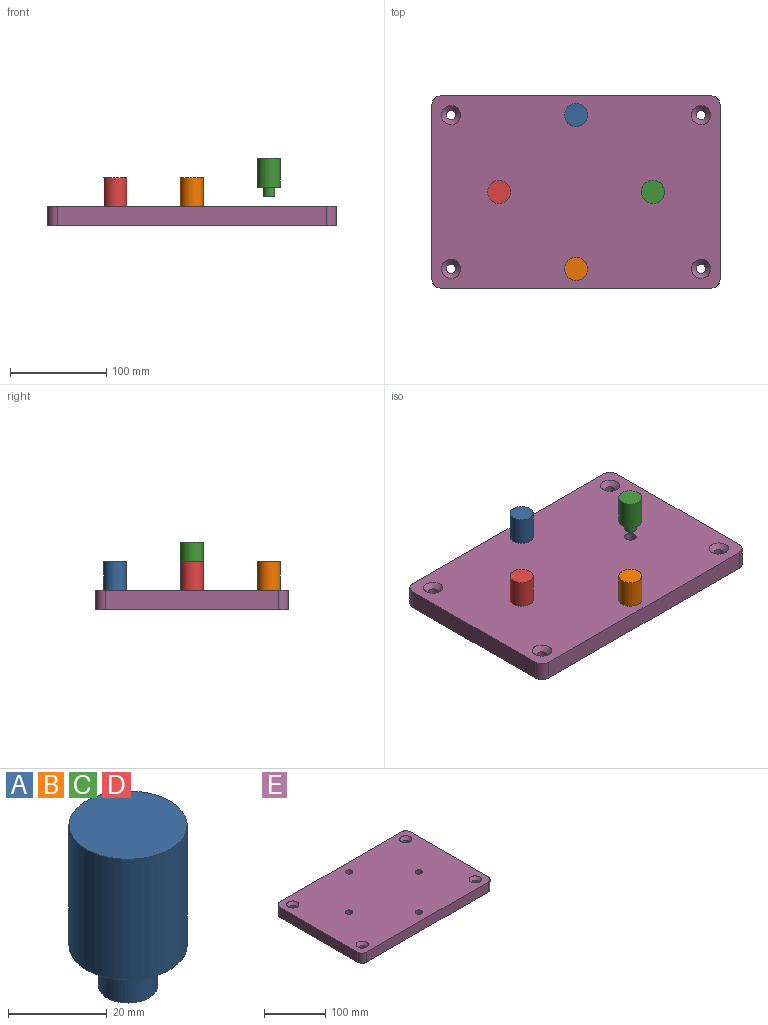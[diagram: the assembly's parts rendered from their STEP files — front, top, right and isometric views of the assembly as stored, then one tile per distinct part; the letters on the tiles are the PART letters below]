
ASSEMBLY  parts=5 mates=4
PART A: 5 faces, bbox 24x24x40 mm
  f0: plane 12x12mm, normal (0,0,-1), area 113.1mm2, adj f1
  f1: cylinder r=6mm len=12mm, axis (0,0,1), area 377mm2, adj f0,f2
  f2: plane 24x24mm, normal (0,0,-1), area 339.3mm2, adj f1,f3
  f3: cylinder r=12mm len=30mm, axis (0,0,1), area 2261.9mm2, adj f2,f4
  f4: plane 24x24mm, normal (0,0,1), area 452.4mm2, adj f3
PART B: same geometry as A
PART C: same geometry as A
PART D: same geometry as A
PART E: 26 faces, bbox 300x200x20 mm
  f0: plane 180x20mm, normal (1,0,0), area 3600mm2, adj f4,f5,f10,f13
  f1: plane 280x20mm, normal (0,1,0), area 5600mm2, adj f4,f5,f10,f11
  f2: plane 180x20mm, normal (-1,0,0), area 3600mm2, adj f4,f5,f11,f12
  f3: plane 280x20mm, normal (0,-1,0), area 5600mm2, adj f4,f5,f12,f13
  f4: plane 300x200mm, normal (0,0,1), area 58205.1mm2, adj f0,f1,f2,f3,f10,f11,f12,f13
  f5: plane 300x200mm, normal (0,0,-1), area 59600mm2, adj f0,f1,f2,f3,f6,f7,f8,f9
  f6: cylinder r=5mm len=15mm, axis (0,0,1), area 471.2mm2, adj f5,f17
  f7: cylinder r=5mm len=15mm, axis (0,0,1), area 471.2mm2, adj f5,f15
  f8: cylinder r=5mm len=15mm, axis (0,0,1), area 471.2mm2, adj f5,f16
  f9: cylinder r=5mm len=15mm, axis (0,0,1), area 471.2mm2, adj f5,f14
  f10: cylinder r=10mm len=20mm, axis (0,0,1), area 314.2mm2, adj f0,f1,f4,f5
  f11: cylinder r=10mm len=20mm, axis (0,0,-1), area 314.2mm2, adj f1,f2,f4,f5
  f12: cylinder r=10mm len=20mm, axis (0,0,1), area 314.2mm2, adj f2,f3,f4,f5
  f13: cylinder r=10mm len=20mm, axis (0,0,-1), area 314.2mm2, adj f0,f3,f4,f5
  f14: cone r=5mm half-angle=45deg, axis (0,0,1), area 333.2mm2, adj f4,f9
  f15: cone r=5mm half-angle=45deg, axis (0,0,1), area 333.2mm2, adj f4,f7
  f16: cone r=5mm half-angle=45deg, axis (0,0,1), area 333.2mm2, adj f4,f8
  f17: cone r=5mm half-angle=45deg, axis (0,0,1), area 333.2mm2, adj f4,f6
  f18: cylinder r=6mm len=12mm, axis (0,0,1), area 377mm2, adj f4,f19
  f19: plane 12x12mm, normal (0,0,1), area 113.1mm2, adj f18
  f20: cylinder r=6mm len=12mm, axis (0,0,1), area 377mm2, adj f4,f21
  f21: plane 12x12mm, normal (0,0,1), area 113.1mm2, adj f20
  f22: cylinder r=6mm len=12mm, axis (0,0,1), area 377mm2, adj f4,f23
  f23: plane 12x12mm, normal (0,0,1), area 113.1mm2, adj f22
  f24: cylinder r=6mm len=12mm, axis (0,0,1), area 377mm2, adj f4,f25
  f25: plane 12x12mm, normal (0,0,1), area 113.1mm2, adj f24
PLACE A t=(-25.81,45.3,-48.7)mm
PLACE B t=(-25.81,-114.7,-48.7)mm
PLACE C rot(axis=(0,0,-1),90deg) t=(54.19,-34.7,-28.7)mm
PLACE D t=(-105.81,-34.7,-48.7)mm
PLACE E t=(-25.81,-34.7,-48.7)mm fixed
MATE fastened A.f1 <-> E.f24  axis (0,0,-1) through (-25.81,45.3,-48.7)mm
MATE fastened B.f1 <-> E.f20  axis (0,0,-1) through (-25.81,-114.7,-48.7)mm
MATE fastened C.f1 <-> E.f22  axis (0,0,-1) through (54.19,-34.7,-28.7)mm
MATE fastened D.f1 <-> E.f18  axis (0,0,-1) through (-105.81,-34.7,-48.7)mm
